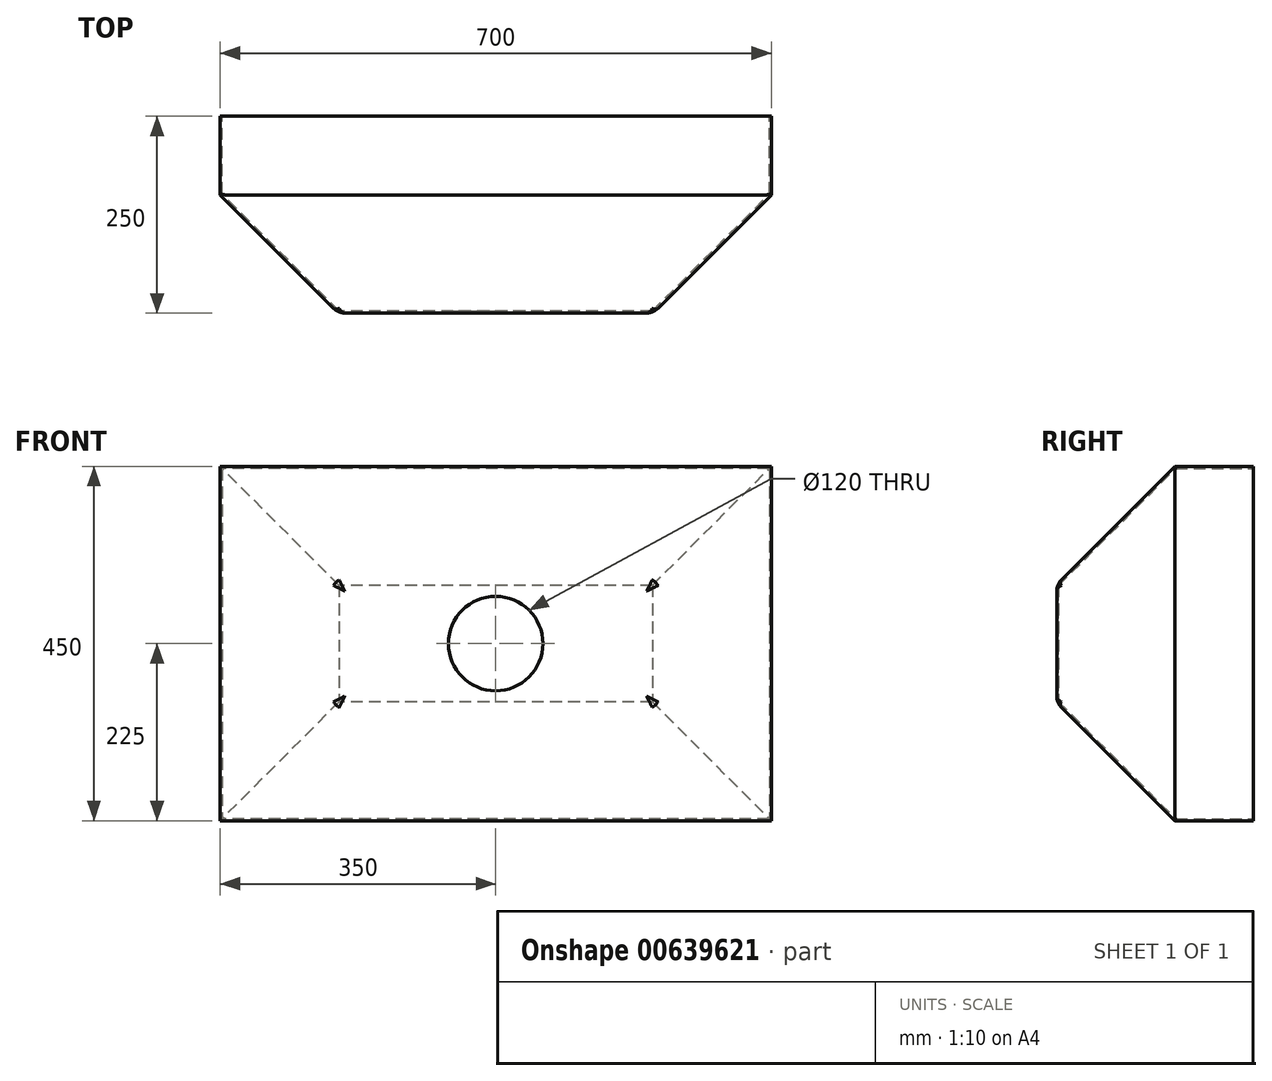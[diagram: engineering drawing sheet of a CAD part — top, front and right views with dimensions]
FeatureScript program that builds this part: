
annotation { "Feature Type Name" : "Feature", "Feature Type Description" : "" }
export const myFeature = defineFeature(function(context is Context, id is Id, definition is map)
    precondition{}
    {
        {
            var Q0;
            Q0=qCreatedBy(makeId("Front.planeOp"),FACE);
            var sketch = newSketch(context, id + "F0", { "sketchPlane" : qUnion([Q0])});
            skLineSegment(sketch, "E0.bottom", {"start": v(350, 225) * mm, "end": v(-350, 225) * mm});
            skLineSegment(sketch, "E0.top", {"start": v(350, -225) * mm, "end": v(-350, -225) * mm});
            skLineSegment(sketch, "E0.left", {"start": v(350, 225) * mm, "end": v(350, -225) * mm});
            skLineSegment(sketch, "E0.right", {"start": v(-350, 225) * mm, "end": v(-350, -225) * mm});
            skPoint(sketch, "E0.middle", {"position": v(0, 0) * mm});
            skSolve(sketch);
        }
        {
            var Q0;
            Q0=makeQuery(id+"F0.imprint","IMPRINT",FACE,{"disambiguationData":[TD([[makeQuery(id+"F0.imprint","IMPRINT",EDGE,{"derivedFrom":sQuery(id+"F0.wireOp",EDGE,"E0.bottom")}),1.0]])]});
            extrude(context, id + "F1", {"entities" : qUnion([Q0]), "depth" : 250 * mm, "offsetDistance" : 25 * mm});
        }
        {
            var Q0;
            Q0=makeQuery(id+"F1.opExtrude","CAP_EDGE",EDGE,{"disambiguationData":[OSD([sQuery(id+"F0.wireOp",EDGE,"E0.right")])],"isStart":false});
            var Q1;
            Q1=makeQuery(id+"F1.opExtrude","CAP_EDGE",EDGE,{"disambiguationData":[OSD([sQuery(id+"F0.wireOp",EDGE,"E0.left")])],"isStart":false});
            chamfer(context, id + "F2", {"entities" : qUnion([Q0, Q1]), "width" : 150 * mm, "tangentPropagation" : true});
        }
        {
            var Q0;
            Q0=makeQuery(id+"F1.opExtrude","CAP_EDGE",EDGE,{"disambiguationData":[OSD([sQuery(id+"F0.wireOp",EDGE,"E0.bottom")])],"isStart":false});
            var Q1;
            Q1=makeQuery(id+"F1.opExtrude","CAP_EDGE",EDGE,{"disambiguationData":[OSD([sQuery(id+"F0.wireOp",EDGE,"E0.top")])],"isStart":false});
            chamfer(context, id + "F3", {"entities" : qUnion([Q0, Q1]), "width" : 150 * mm, "tangentPropagation" : true});
        }
        {
            var Q0;
            Q0=makeQuery(id+"F1.opExtrude","CAP_FACE",FACE,{"disambiguationData":[OSD([sQuery(id+"F0.wireOp",EDGE,"E0.bottom"),sQuery(id+"F0.wireOp",EDGE,"E0.top"),sQuery(id+"F0.wireOp",EDGE,"E0.left"),sQuery(id+"F0.wireOp",EDGE,"E0.right")])],"isStart":true});
            shell(context, id + "F4", {"entities" : qUnion([Q0]), "thickness" : 2.5 * mm});
        }
        {
            var Q0;
            Q0=makeQuery(id+"F1.opExtrude","CAP_FACE",FACE,{"disambiguationData":[OSD([sQuery(id+"F0.wireOp",EDGE,"E0.bottom"),sQuery(id+"F0.wireOp",EDGE,"E0.top"),sQuery(id+"F0.wireOp",EDGE,"E0.left"),sQuery(id+"F0.wireOp",EDGE,"E0.right")])],"isStart":false});
            var sketch = newSketch(context, id + "F5", { "sketchPlane" : qUnion([Q0])});
            skCircle(sketch, "E1", {"center": v(0, 0) * mm, "radius": 60 * mm});
            skSolve(sketch);
        }
        {
            var Q0;
            Q0=makeQuery(id+"F5.imprint","IMPRINT",FACE,{"disambiguationData":[TD([[makeQuery(id+"F5.imprint","IMPRINT",EDGE,{"derivedFrom":sQuery(id+"F5.wireOp",EDGE,"E1")}),1.0]])]});
            extrude(context, id + "F6", {"entities" : qUnion([Q0]), "operationType" : NewBodyOperationType.REMOVE, "endBound" : BoundingType.THROUGH_ALL, "oppositeDirection" : true, "depth" : 70 * mm, "offsetDistance" : 25 * mm});
        }
        {
            var Q0;
            Q0=qCreatedBy(makeId("Top.planeOp"),FACE);
            var sketch = newSketch(context, id + "F7", { "sketchPlane" : qUnion([Q0])});
            skPoint(sketch, "E2", {"position": v(0, -254.17) * mm});
            skLineSegment(sketch, "E3", {"start": v(0, -254.17) * mm, "end": v(0, -597.21) * mm});
            skLineSegment(sketch, "E4", {"start": v(-130, -727.21) * mm, "end": v(-560, -727.21) * mm});
            skPoint(sketch, "E5.visualSharp", {"position": v(0, -727.21) * mm});
            skArc(sketch, "E5.filletArc", {"start": v(-130, -727.21) * mm, "mid": v(-38.08, -689.14) * mm, "end": v(0, -597.21) * mm});
            skSolve(sketch);
        }
        {
            var Q0;
            Q0=qCreatedBy(makeId("Right.planeOp"),FACE);
            cPlane(context, id + "F8", {"entities" : qUnion([Q0]), "cplaneType" : CPlaneType.OFFSET, "offset" : 555 * mm, "oppositeDirection" : true, "width" : 150 * mm, "height" : 150 * mm});
        }
        {
            var Q0;
            Q0=qCreatedBy(id+"F8.planeOp",FACE);
            var sketch = newSketch(context, id + "F9", { "sketchPlane" : qUnion([Q0])});
            skCircle(sketch, "E6", {"center": v(-727.21, 0) * mm, "radius": 60 * mm});
            skSolve(sketch);
        }
        {
            var Q0;
            Q0=makeQuery(id+"F3.opChamfer","BLEND_EDGE",EDGE,{"blendedFrom":[makeQuery(id+"F1.opExtrude","CAP_EDGE",EDGE,{"disambiguationData":[OSD([sQuery(id+"F0.wireOp",EDGE,"E0.top")])],"isStart":false}),makeQuery(id+"F2.opChamfer","BLEND_FACE",FACE,{"disambiguationData":[OSD([sQuery(id+"F0.wireOp",EDGE,"E0.left")])]})],"blendedInto":[makeQuery(id+"F2.opChamfer","BLEND_FACE",FACE,{"disambiguationData":[OSD([sQuery(id+"F0.wireOp",EDGE,"E0.left")])]})]});
            fillet(context, id + "F10", {"entities" : qUnion([Q0]), "radius" : 10 * mm, "tangentPropagation" : true, "allowEdgeOverflow" : false});
        }
        {
            var Q0;
            Q0=makeQuery(id+"F3.opChamfer","BLEND_EDGE",EDGE,{"blendedFrom":[makeQuery(id+"F1.opExtrude","CAP_EDGE",EDGE,{"disambiguationData":[OSD([sQuery(id+"F0.wireOp",EDGE,"E0.top")])],"isStart":false}),makeQuery(id+"F2.opChamfer","BLEND_FACE",FACE,{"disambiguationData":[OSD([sQuery(id+"F0.wireOp",EDGE,"E0.right")])]})],"blendedInto":[makeQuery(id+"F2.opChamfer","BLEND_FACE",FACE,{"disambiguationData":[OSD([sQuery(id+"F0.wireOp",EDGE,"E0.right")])]})]});
            var Q1;
            Q1=makeQuery(id+"F3.opChamfer","BLEND_EDGE",EDGE,{"blendedFrom":[makeQuery(id+"F1.opExtrude","CAP_EDGE",EDGE,{"disambiguationData":[OSD([sQuery(id+"F0.wireOp",EDGE,"E0.bottom")])],"isStart":false}),makeQuery(id+"F2.opChamfer","BLEND_FACE",FACE,{"disambiguationData":[OSD([sQuery(id+"F0.wireOp",EDGE,"E0.left")])]})],"blendedInto":[makeQuery(id+"F2.opChamfer","BLEND_FACE",FACE,{"disambiguationData":[OSD([sQuery(id+"F0.wireOp",EDGE,"E0.left")])]})]});
            var Q2;
            Q2=makeQuery(id+"F3.opChamfer","BLEND_EDGE",EDGE,{"blendedFrom":[makeQuery(id+"F1.opExtrude","CAP_EDGE",EDGE,{"disambiguationData":[OSD([sQuery(id+"F0.wireOp",EDGE,"E0.bottom")])],"isStart":false}),makeQuery(id+"F2.opChamfer","BLEND_FACE",FACE,{"disambiguationData":[OSD([sQuery(id+"F0.wireOp",EDGE,"E0.right")])]})],"blendedInto":[makeQuery(id+"F2.opChamfer","BLEND_FACE",FACE,{"disambiguationData":[OSD([sQuery(id+"F0.wireOp",EDGE,"E0.right")])]})]});
            fillet(context, id + "F11", {"entities" : qUnion([Q0, Q1, Q2]), "radius" : 10 * mm, "tangentPropagation" : true, "allowEdgeOverflow" : false});
        }
        {
            var Q0;
            {var subQ0=sQuery(id+"F0.wireOp",EDGE,"E0.right");Q0=makeQuery(id+"F2.opChamfer","BLEND_EDGE",EDGE,{"blendedFrom":[makeQuery(id+"F1.opExtrude","CAP_EDGE",EDGE,{"disambiguationData":[OSD([subQ0])],"isStart":false}),makeQuery(id+"F1.opExtrude","CAP_FACE",FACE,{"disambiguationData":[OSD([sQuery(id+"F0.wireOp",EDGE,"E0.bottom"),sQuery(id+"F0.wireOp",EDGE,"E0.top"),sQuery(id+"F0.wireOp",EDGE,"E0.left"),subQ0])],"isStart":false})],"blendedInto":[makeQuery(id+"F1.opExtrude","CAP_FACE",FACE,{"disambiguationData":[OSD([sQuery(id+"F0.wireOp",EDGE,"E0.bottom"),sQuery(id+"F0.wireOp",EDGE,"E0.top"),sQuery(id+"F0.wireOp",EDGE,"E0.left"),subQ0])],"isStart":false})]});}
            fillet(context, id + "F12", {"entities" : qUnion([Q0]), "radius" : 20 * mm, "tangentPropagation" : true, "allowEdgeOverflow" : false});
        }
        {
            var Q0;
            Q0=qCreatedBy(makeId("Front.planeOp"),FACE);
            var sketch = newSketch(context, id + "F13", { "sketchPlane" : qUnion([Q0])});
            skLineSegment(sketch, "E7", {"start": v(-558.44, 0) * mm, "end": v(-612.27, 0) * mm});
            skLineSegment(sketch, "E8", {"start": v(-712.27, -100) * mm, "end": v(-712.27, -888.35) * mm});
            skPoint(sketch, "E9.visualSharp", {"position": v(-712.27, 0) * mm});
            skArc(sketch, "E9.filletArc", {"start": v(-612.27, 0) * mm, "mid": v(-682.98, -29.29) * mm, "end": v(-712.27, -100) * mm});
            skSolve(sketch);
        }
    });
